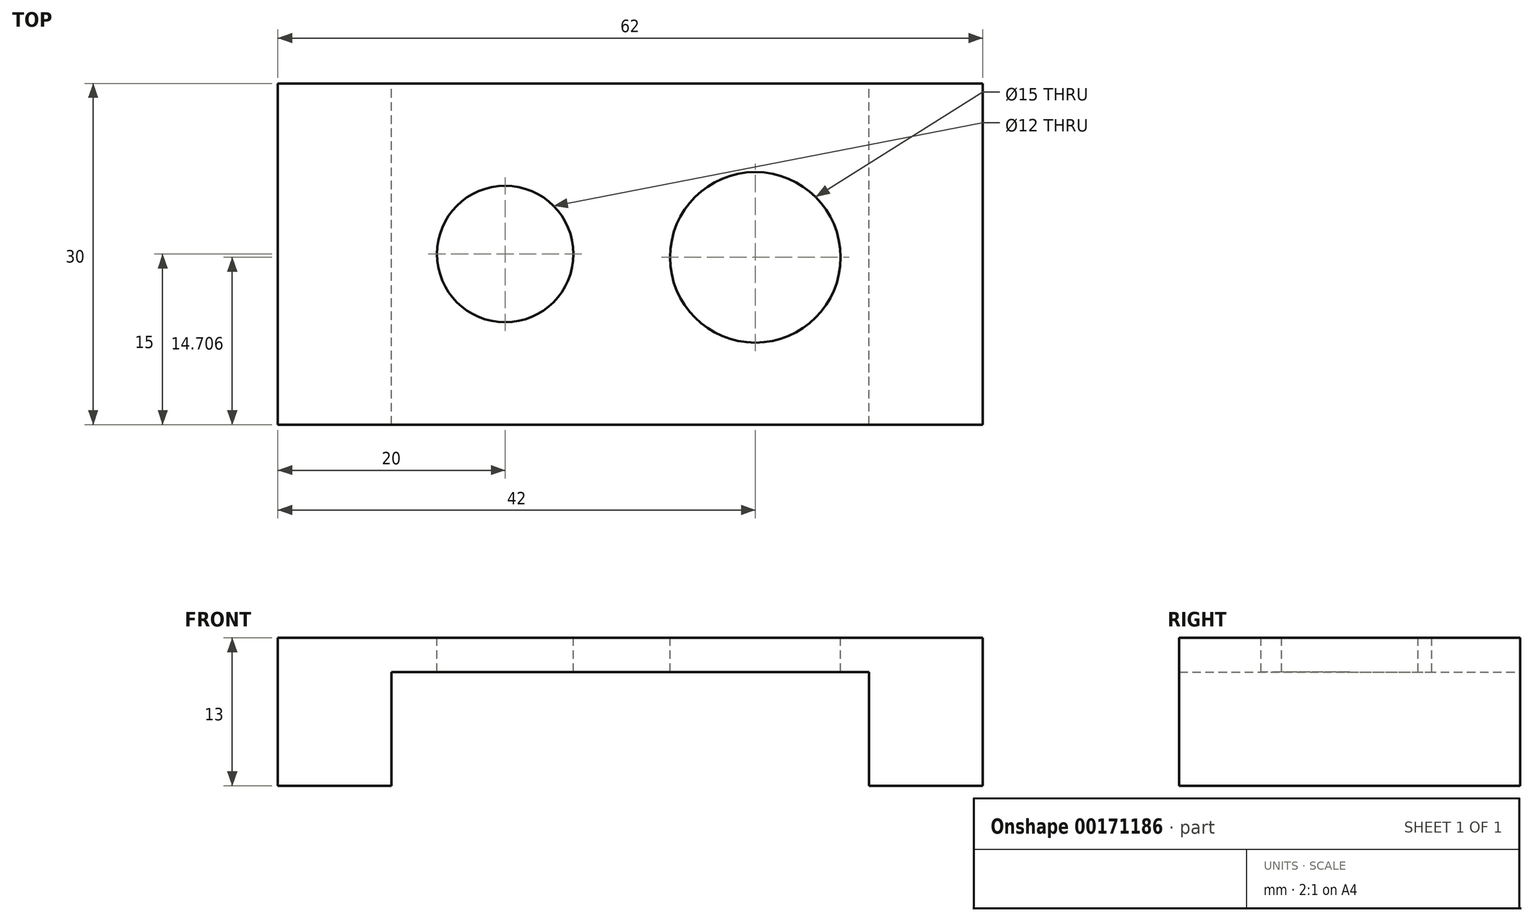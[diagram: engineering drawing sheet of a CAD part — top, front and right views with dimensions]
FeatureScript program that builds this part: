
annotation { "Feature Type Name" : "Feature", "Feature Type Description" : "" }
export const myFeature = defineFeature(function(context is Context, id is Id, definition is map)
    precondition{}
    {
        {
            var Q0;
            Q0=qCreatedBy(makeId("Front.planeOp"),FACE);
            var sketch = newSketch(context, id + "F0", { "sketchPlane" : qUnion([Q0])});
            skLineSegment(sketch, "E0", {"start": v(0, 0) * mm, "end": v(62, 0) * mm});
            skLineSegment(sketch, "E1", {"start": v(62, 0) * mm, "end": v(62, -13) * mm});
            skLineSegment(sketch, "E2", {"start": v(62, -13) * mm, "end": v(52, -13) * mm});
            skLineSegment(sketch, "E3", {"start": v(52, -13) * mm, "end": v(52, -3) * mm});
            skLineSegment(sketch, "E4", {"start": v(52, -3) * mm, "end": v(10, -3) * mm});
            skLineSegment(sketch, "E5", {"start": v(10, -3) * mm, "end": v(10, -13) * mm});
            skLineSegment(sketch, "E6", {"start": v(10, -13) * mm, "end": v(0, -13) * mm});
            skLineSegment(sketch, "E7", {"start": v(0, -13) * mm, "end": v(0, 0) * mm});
            skSolve(sketch);
        }
        {
            var Q0;
            Q0=makeQuery(id+"F0.imprint","IMPRINT",FACE,{"disambiguationData":[TD([[makeQuery(id+"F0.imprint","IMPRINT",EDGE,{"derivedFrom":sQuery(id+"F0.wireOp",EDGE,"E0")}),-1.0]])]});
            extrude(context, id + "F1", {"entities" : qUnion([Q0]), "depth" : 30 * mm});
        }
        {
            var Q0;
            Q0=makeQuery(id+"F1.opExtrude","SWEPT_FACE",FACE,{"disambiguationData":[OSD([sQuery(id+"F0.wireOp",EDGE,"E0")])]});
            var sketch = newSketch(context, id + "F2", { "sketchPlane" : qUnion([Q0])});
            skSolve(sketch);
        }
        {
            var Q0;
            {var subQ0=sQuery(id+"F0.wireOp",EDGE,"E0");Q0=makeQuery(id+"F2.imprint","IMPRINT",FACE,{"disambiguationData":[TD([[makeQuery(id+"F2.imprint","IMPRINT",EDGE,{"derivedFrom":makeQuery(id+"F1.opExtrude","CAP_EDGE",EDGE,{"disambiguationData":[OSD([subQ0])],"isStart":true})}),-1.0]])]});}
            var sketch = newSketch(context, id + "F3", { "sketchPlane" : qUnion([Q0])});
            skCircle(sketch, "E8", {"center": v(20, -15) * mm, "radius": 6 * mm});
            skCircle(sketch, "E9", {"center": v(42, -15.3) * mm, "radius": 7.5 * mm});
            skSolve(sketch);
        }
        {
            var Q0;
            Q0 = qSketchRegion(id + "F3", true);
            extrude(context, id + "F4", {"entities" : qUnion([Q0]), "operationType" : NewBodyOperationType.REMOVE, "endBound" : BoundingType.THROUGH_ALL, "oppositeDirection" : true, "depth" : 25 * mm});
        }
    });
